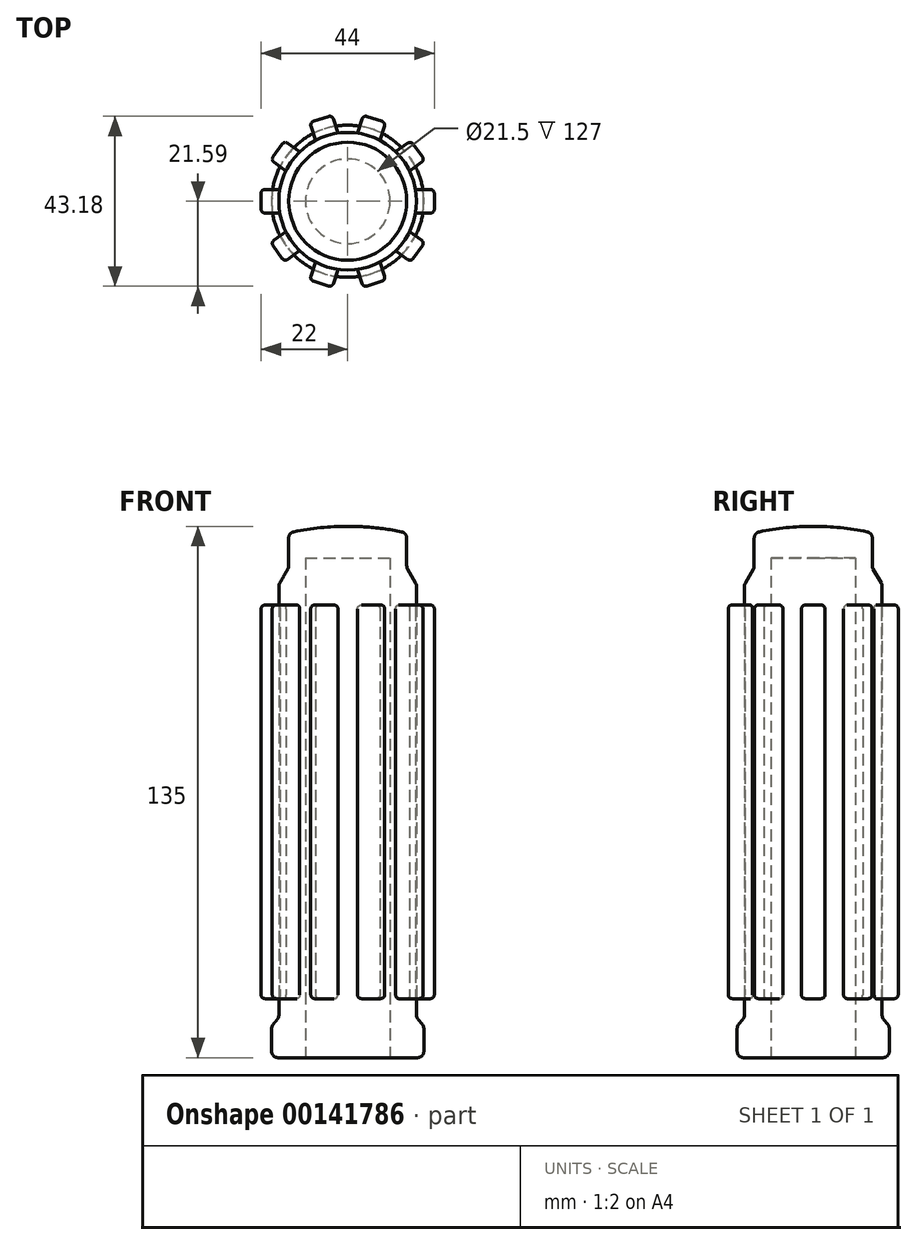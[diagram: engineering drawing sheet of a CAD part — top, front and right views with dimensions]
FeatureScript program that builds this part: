
annotation { "Feature Type Name" : "Feature", "Feature Type Description" : "" }
export const myFeature = defineFeature(function(context is Context, id is Id, definition is map)
    precondition{}
    {
        {
            var Q0;
            Q0=qCreatedBy(makeId("Front.planeOp"),FACE);
            var sketch = newSketch(context, id + "F0", { "sketchPlane" : qUnion([Q0])});
            skLineSegment(sketch, "E0", {"start": v(10.75, 0) * mm, "end": v(19.32, 0) * mm});
            skLineSegment(sketch, "E1", {"start": v(19.32, 0) * mm, "end": v(19.32, 8) * mm});
            skLineSegment(sketch, "E2", {"start": v(19.32, 8) * mm, "end": v(17.5, 10.17) * mm});
            skLineSegment(sketch, "E3", {"start": v(17.5, 10.17) * mm, "end": v(17.5, 120.17) * mm});
            skLineSegment(sketch, "E4", {"start": v(17.5, 120.17) * mm, "end": v(15, 124.5) * mm});
            skLineSegment(sketch, "E5", {"start": v(15, 124.5) * mm, "end": v(15, 133.32) * mm});
            skArc(sketch, "E6", {"start": v(15, 133.32) * mm, "mid": v(7.55, 134.58) * mm, "end": v(0, 135) * mm});
            skLineSegment(sketch, "E7", {"start": v(0, 135) * mm, "end": v(0, 127) * mm});
            skLineSegment(sketch, "E8", {"start": v(0, 127) * mm, "end": v(10.75, 127) * mm});
            skLineSegment(sketch, "E9", {"start": v(10.75, 127) * mm, "end": v(10.75, 0) * mm});
            skLineSegment(sketch, "E10", {"start": v(0, 0) * mm, "end": v(0, 150.38) * mm, "construction": true});
            skSolve(sketch);
        }
        {
            var Q0;
            Q0 = qSketchRegion(id + "F0", true);
            var Q1;
            Q1=sQuery(id+"F0.wireOp",EDGE,"E10");
            revolve(context, id + "F1", {"entities" : qUnion([Q0]), "axis" : qUnion([Q1]), "revolveType" : RevolveType.FULL});
        }
        {
            var Q0;
            Q0=makeQuery(id+"F1.opRevolve","SWEPT_EDGE",EDGE,{"disambiguationData":[OSD([sQuery(id+"F0.wireOp",EDGE,"E5"),sQuery(id+"F0.wireOp",EDGE,"E6")])]});
            var Q1;
            Q1=makeQuery(id+"F1.opRevolve","SWEPT_EDGE",EDGE,{"disambiguationData":[OSD([sQuery(id+"F0.wireOp",EDGE,"E4"),sQuery(id+"F0.wireOp",EDGE,"E5")])]});
            var Q2;
            Q2=makeQuery(id+"F1.opRevolve","SWEPT_EDGE",EDGE,{"disambiguationData":[OSD([sQuery(id+"F0.wireOp",EDGE,"E3"),sQuery(id+"F0.wireOp",EDGE,"E4")])]});
            var Q3;
            Q3=makeQuery(id+"F1.opRevolve","SWEPT_EDGE",EDGE,{"disambiguationData":[OSD([sQuery(id+"F0.wireOp",EDGE,"E2"),sQuery(id+"F0.wireOp",EDGE,"E3")])]});
            var Q4;
            Q4=makeQuery(id+"F1.opRevolve","SWEPT_EDGE",EDGE,{"disambiguationData":[OSD([sQuery(id+"F0.wireOp",EDGE,"E1"),sQuery(id+"F0.wireOp",EDGE,"E2")])]});
            var Q5;
            Q5=makeQuery(id+"F1.opRevolve","SWEPT_EDGE",EDGE,{"disambiguationData":[OSD([sQuery(id+"F0.wireOp",EDGE,"E0"),sQuery(id+"F0.wireOp",EDGE,"E1")])]});
            fillet(context, id + "F2", {"entities" : qUnion([Q0, Q1, Q2, Q3, Q4, Q5]), "radius" : 1.6 * mm, "tangentPropagation" : true, "allowEdgeOverflow" : false});
        }
        {
            var Q0;
            Q0=qCreatedBy(makeId("Right.planeOp"),FACE);
            cPlane(context, id + "F3", {"entities" : qUnion([Q0]), "cplaneType" : CPlaneType.OFFSET, "offset" : 22 * mm, "width" : 150 * mm, "height" : 150 * mm});
        }
        {
            var Q0;
            Q0=qCreatedBy(id+"F3.planeOp",FACE);
            var sketch = newSketch(context, id + "F4", { "sketchPlane" : qUnion([Q0])});
            skLineSegment(sketch, "E11.bottom", {"start": v(-3, 115) * mm, "end": v(3, 115) * mm});
            skLineSegment(sketch, "E11.top", {"start": v(-3, 15) * mm, "end": v(3, 15) * mm});
            skLineSegment(sketch, "E11.left", {"start": v(-3, 115) * mm, "end": v(-3, 15) * mm});
            skLineSegment(sketch, "E11.right", {"start": v(3, 115) * mm, "end": v(3, 15) * mm});
            skSolve(sketch);
        }
        {
            var Q0;
            Q0 = qSketchRegion(id + "F4", true);
            var Q1;
            Q1=makeQuery(id+"F1.opRevolve","SWEPT_FACE",FACE,{"disambiguationData":[OSD([sQuery(id+"F0.wireOp",EDGE,"E3")])]});
            extrude(context, id + "F5", {"entities" : qUnion([Q0]), "endBound" : BoundingType.UP_TO_SURFACE, "oppositeDirection" : true, "endBoundEntityFace" : qUnion([Q1]), "depth" : 25 * mm});
        }
        {
            var Q0;
            Q0=makeQuery(id+"F5.opExtrude","SWEPT_EDGE",EDGE,{"disambiguationData":[OSD([sQuery(id+"F4.wireOp",EDGE,"E11.bottom"),sQuery(id+"F4.wireOp",EDGE,"E11.left")])]});
            var Q1;
            Q1=makeQuery(id+"F5.opExtrude","SWEPT_EDGE",EDGE,{"disambiguationData":[OSD([sQuery(id+"F4.wireOp",EDGE,"E11.bottom"),sQuery(id+"F4.wireOp",EDGE,"E11.right")])]});
            var Q2;
            Q2=makeQuery(id+"F5.opExtrude","CAP_EDGE",EDGE,{"disambiguationData":[OSD([sQuery(id+"F4.wireOp",EDGE,"E11.bottom")])],"isStart":true});
            var Q3;
            Q3=makeQuery(id+"F5.opExtrude","CAP_EDGE",EDGE,{"disambiguationData":[OSD([sQuery(id+"F4.wireOp",EDGE,"E11.left")])],"isStart":true});
            var Q4;
            Q4=makeQuery(id+"F5.opExtrude","CAP_EDGE",EDGE,{"disambiguationData":[OSD([sQuery(id+"F4.wireOp",EDGE,"E11.right")])],"isStart":true});
            var Q5;
            Q5=makeQuery(id+"F5.opExtrude","CAP_EDGE",EDGE,{"disambiguationData":[OSD([sQuery(id+"F4.wireOp",EDGE,"E11.top")])],"isStart":true});
            var Q6;
            Q6=makeQuery(id+"F5.opExtrude","SWEPT_EDGE",EDGE,{"disambiguationData":[OSD([sQuery(id+"F4.wireOp",EDGE,"E11.top"),sQuery(id+"F4.wireOp",EDGE,"E11.right")])]});
            var Q7;
            Q7=makeQuery(id+"F5.opExtrude","SWEPT_EDGE",EDGE,{"disambiguationData":[OSD([sQuery(id+"F4.wireOp",EDGE,"E11.top"),sQuery(id+"F4.wireOp",EDGE,"E11.left")])]});
            fillet(context, id + "F6", {"entities" : qUnion([Q0, Q1, Q2, Q3, Q4, Q5, Q6, Q7]), "radius" : 1 * mm, "tangentPropagation" : true, "allowEdgeOverflow" : false});
        }
        {
            var Q0;
            Q0=makeQuery(id+"F5.opExtrude","SWEPT_BODY",BODY,{"disambiguationData":[OSD([sQuery(id+"F4.wireOp",EDGE,"E11.bottom"),sQuery(id+"F4.wireOp",EDGE,"E11.top"),sQuery(id+"F4.wireOp",EDGE,"E11.left"),sQuery(id+"F4.wireOp",EDGE,"E11.right")])]});
            var Q1;
            Q1=sQuery(id+"F0.wireOp",EDGE,"E10");
            circularPattern(context, id + "F7", {"entities" : qUnion([Q0]), "axis" : qUnion([Q1]), "angle" : 360 * degree, "instanceCount" : 10, "equalSpace" : true});
        }
    });
